# Revit family: Geometric_Table_BIM
name_source: partatom
category: Arredi
units: mm (PartAtom-declared; Revit-internal decimal feet)

## family parameters
Attiva taglio nelle viste = No
Basato su piano di lavoro = No
Condiviso = No
Numero OmniClass = 23.40.20.00
Origine composizione di rendering = Geometria famiglia
Punto di calcolo locali = No
Sempre verticale = Sì
Taglio con vuoti quando caricato = No
Titolo OmniClass = General Furniture and Specialties

## types (1)
- CB-464
    AVAILABLE FINISHES = Ebonized black lacquer on Ash (EB) or bleached, white pigment, matte acrylic on Ash (BL). Raw effect lacquer on Oak (RE). Hand rubbed natural oil on Oak or Walnut (NA), or hand rubbed black oil on Walnut (BO). Base: Tubular steel with smoke powder coat finish (SP), or satin nickel (SN), satin brass (SB), bronze (BZ) or gunmetal (GM) nanoceramic coated tubular steel.
    BASE MATERIAL = BASSAM_FELLOWS_WALNUT_BLACK_OIL_W-BO
    BIM BADGE = https://bim.archiproducts.com
    COLLECTION = Geometric
    DIAMETER = 1550 mm  [stored 5.0853 ft]
    Descrizione = Round steel and wood dining table
    FEET MATERIAL = BASSAM_FELLOWS_BRONZE_BZ
    HEIGHT = 720 mm
    MATERIAL DESCRIPTION = Wood veneer with solid wood edge top. Tubular stainless steel base.
    Modello = Geometric Dining Table
    PRODUCT CODE = CB-464
    PRODUCT SHEET = https://www.archiproducts.com
    Produttore = BassamFellows
    Prospetto di default = 0 mm  [stored 0 ft]
    TECHNICAL SHEET = https://bassamfellows.com
    URL = https://bassamfellows.com

note: [stored X ft] marks values corroborated as IEEE doubles in the binary element streams (Revit-internal decimal feet)

## geometry (parser evidence)
native form markers: Sweep x2
no freeform markers — native parametric forms only
